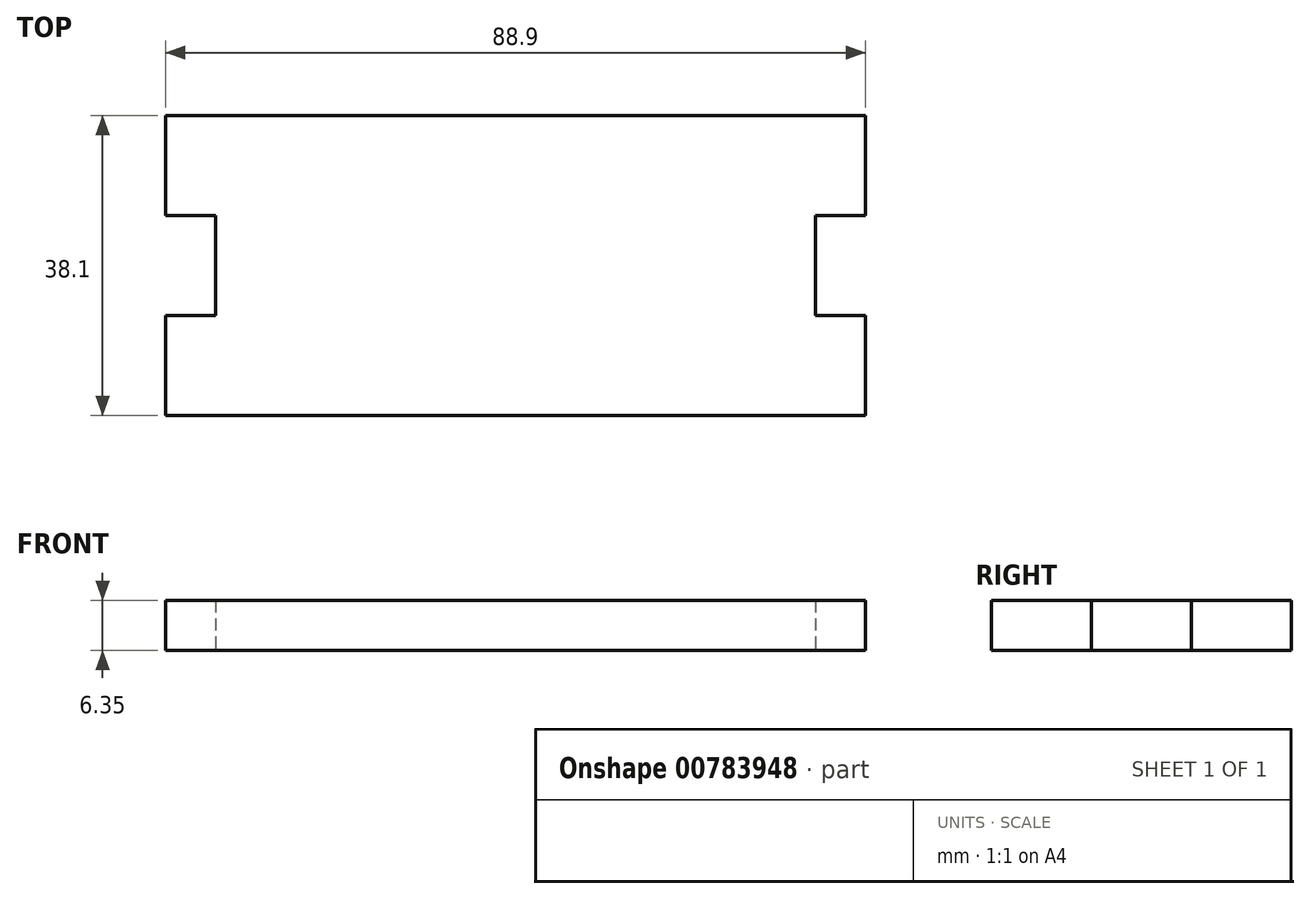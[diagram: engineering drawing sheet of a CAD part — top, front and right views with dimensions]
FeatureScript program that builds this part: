
annotation { "Feature Type Name" : "Feature", "Feature Type Description" : "" }
export const myFeature = defineFeature(function(context is Context, id is Id, definition is map)
    precondition{}
    {
        {
            var Q0;
            Q0=qCreatedBy(makeId("Top.planeOp"),FACE);
            var sketch = newSketch(context, id + "F0", { "sketchPlane" : qUnion([Q0])});
            skLineSegment(sketch, "E0.bottom", {"start": v(38.1, 19.05) * mm, "end": v(-38.1, 19.05) * mm});
            skLineSegment(sketch, "E0.top", {"start": v(38.1, -19.05) * mm, "end": v(-38.1, -19.05) * mm});
            skLineSegment(sketch, "E0.left", {"start": v(38.1, 6.35) * mm, "end": v(38.1, -6.35) * mm});
            skLineSegment(sketch, "E0.right", {"start": v(-38.1, 6.35) * mm, "end": v(-38.1, -6.35) * mm});
            skPoint(sketch, "E0.middle", {"position": v(0, 0) * mm});
            skLineSegment(sketch, "E1.top", {"start": v(-38.1, 6.35) * mm, "end": v(-44.45, 6.35) * mm});
            skLineSegment(sketch, "E2.top", {"start": v(-38.1, -6.35) * mm, "end": v(-44.45, -6.35) * mm});
            skLineSegment(sketch, "E3.top", {"start": v(38.1, 6.35) * mm, "end": v(44.45, 6.35) * mm});
            skLineSegment(sketch, "E4.top", {"start": v(38.1, -6.35) * mm, "end": v(44.45, -6.35) * mm});
            skLineSegment(sketch, "E5", {"start": v(-38.1, 19.05) * mm, "end": v(-44.45, 19.05) * mm});
            skLineSegment(sketch, "E6", {"start": v(-44.45, 19.05) * mm, "end": v(-44.45, 6.35) * mm});
            skLineSegment(sketch, "E7", {"start": v(-44.45, -19.05) * mm, "end": v(-38.1, -19.05) * mm});
            skLineSegment(sketch, "E8", {"start": v(38.1, -19.05) * mm, "end": v(44.45, -19.05) * mm});
            skLineSegment(sketch, "E9", {"start": v(44.45, -19.05) * mm, "end": v(44.45, -6.35) * mm});
            skLineSegment(sketch, "E10", {"start": v(44.45, 19.05) * mm, "end": v(38.1, 19.05) * mm});
            skLineSegment(sketch, "E11.trimOffspring", {"start": v(44.45, 6.35) * mm, "end": v(44.45, 19.05) * mm});
            skLineSegment(sketch, "E12.trimOffspring", {"start": v(-44.45, -6.35) * mm, "end": v(-44.45, -19.05) * mm});
            skSolve(sketch);
        }
        {
            var Q0;
            Q0=makeQuery(id+"F0.imprint","IMPRINT",FACE,{"disambiguationData":[TD([[makeQuery(id+"F0.imprint","IMPRINT",EDGE,{"derivedFrom":sQuery(id+"F0.wireOp",EDGE,"E0.bottom")}),1.0]])]});
            var Q1;
            Q1=makeQuery(id+"F0.imprint","IMPRINT",FACE,{"disambiguationData":[TD([[makeQuery(id+"F0.imprint","IMPRINT",EDGE,{"derivedFrom":sQuery(id+"F0.wireOp",EDGE,"E1.bottom")}),1.0]])]});
            var Q2;
            Q2=makeQuery(id+"F0.imprint","IMPRINT",FACE,{"disambiguationData":[TD([[makeQuery(id+"F0.imprint","IMPRINT",EDGE,{"derivedFrom":sQuery(id+"F0.wireOp",EDGE,"E2.bottom")}),-1.0]])]});
            var Q3;
            Q3=makeQuery(id+"F0.imprint","IMPRINT",FACE,{"disambiguationData":[TD([[makeQuery(id+"F0.imprint","IMPRINT",EDGE,{"derivedFrom":sQuery(id+"F0.wireOp",EDGE,"E4.bottom")}),1.0]])]});
            var Q4;
            Q4=makeQuery(id+"F0.imprint","IMPRINT",FACE,{"disambiguationData":[TD([[makeQuery(id+"F0.imprint","IMPRINT",EDGE,{"derivedFrom":sQuery(id+"F0.wireOp",EDGE,"E3.bottom")}),-1.0]])]});
            var Q5;
            Q5=makeQuery(id+"F0.imprint","IMPRINT",FACE,{"disambiguationData":[TD([[makeQuery(id+"F0.imprint","IMPRINT",EDGE,{"derivedFrom":sQuery(id+"F0.wireOp",EDGE,"E0.left")}),1.0]])]});
            var Q6;
            Q6=makeQuery(id+"F0.imprint","IMPRINT",FACE,{"disambiguationData":[TD([[makeQuery(id+"F0.imprint","IMPRINT",EDGE,{"derivedFrom":sQuery(id+"F0.wireOp",EDGE,"E0.right")}),-1.0]])]});
            extrude(context, id + "F1", {"entities" : qUnion([Q0, Q1, Q2, Q3, Q4, Q5, Q6]), "depth" : 6.35 * mm, "offsetDistance" : 25.4 * mm});
        }
    });
